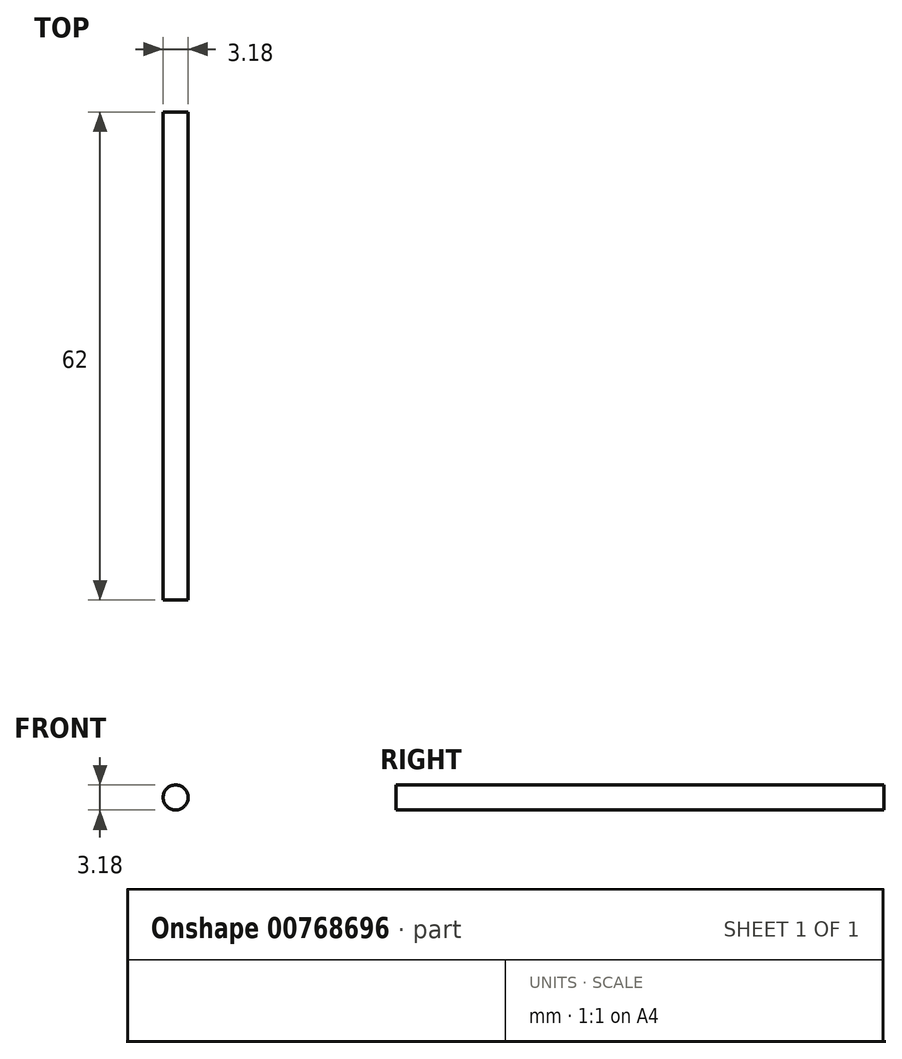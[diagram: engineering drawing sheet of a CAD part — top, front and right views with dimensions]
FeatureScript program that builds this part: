
annotation { "Feature Type Name" : "Feature", "Feature Type Description" : "" }
export const myFeature = defineFeature(function(context is Context, id is Id, definition is map)
    precondition{}
    {
        {
            var Q0;
            Q0=qCreatedBy(makeId("Front.planeOp"),FACE);
            var sketch = newSketch(context, id + "F0", { "sketchPlane" : qUnion([Q0])});
            skCircle(sketch, "E0", {"center": v(0, 0) * mm, "radius": 1.59 * mm});
            skSolve(sketch);
        }
        {
            var Q0;
            Q0=makeQuery(id+"F0.imprint","IMPRINT",FACE,{"disambiguationData":[TD([[makeQuery(id+"F0.imprint","IMPRINT",EDGE,{"derivedFrom":sQuery(id+"F0.wireOp",EDGE,"E0")}),1.0]])]});
            extrude(context, id + "F1", {"entities" : qUnion([Q0]), "depth" : 62 * mm, "offsetDistance" : 25 * mm});
        }
    });
